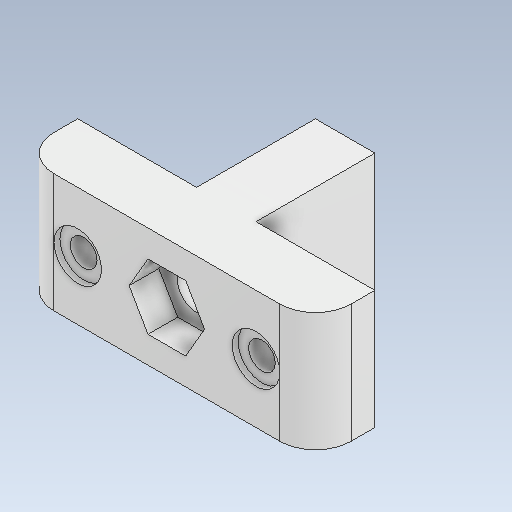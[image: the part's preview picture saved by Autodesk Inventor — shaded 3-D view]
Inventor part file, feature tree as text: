
AUTODESK INVENTOR PART (.ipt)
format: ipt  version: 2020 (Build 240168000, 168)  size: 176,128 bytes
history: native  units: mm
features: extrude x4, sketch x2, other x1, fillet x1
ambient origin geometry x8: Origin, YZ Plane, XZ Plane, XY Plane, X Axis, Y Axis, Z Axis, Center Point
bodies: Body1 (feature_tree)
feature tree (8):
  other  "Bryła1"
  extrude  "Wyciągnięcie proste1"  Depth=20.0mm
  sketch  "Szkic2"
  extrude  "Wyciągnięcie proste2"  Depth=20.0mm
  extrude  "Wyciągnięcie proste3"  Depth=20.0mm
  fillet  "Zaokrąglenie1"  Radius=20.0mm
  extrude  "Wyciągnięcie proste4"  Depth=50.0mm
  sketch  "Szkic1"
